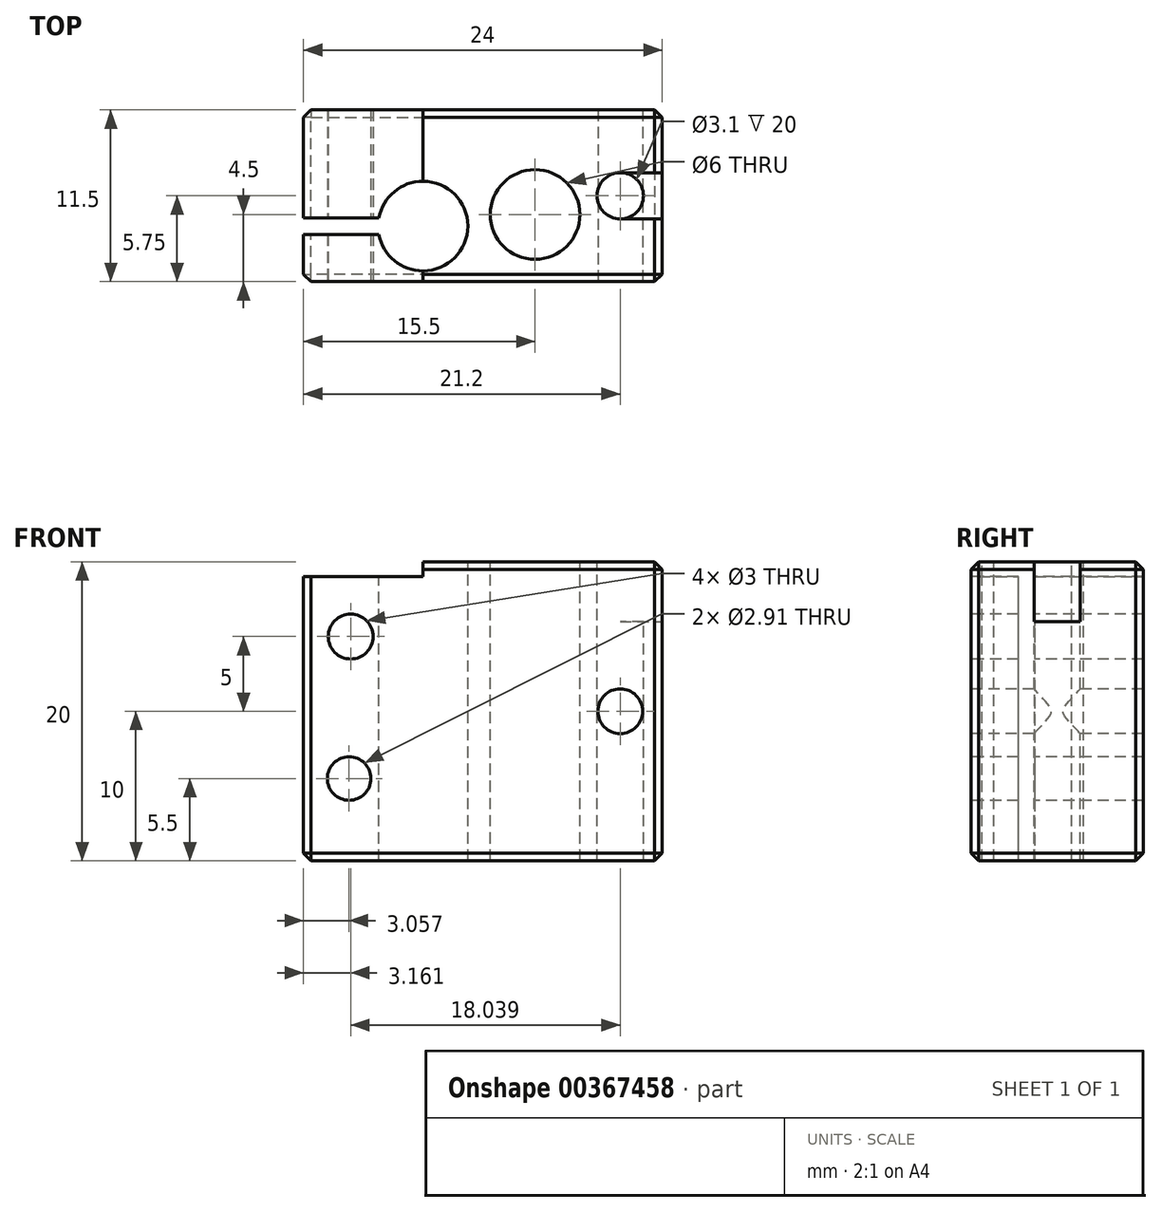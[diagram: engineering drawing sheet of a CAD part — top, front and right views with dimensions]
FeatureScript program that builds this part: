
annotation { "Feature Type Name" : "Feature", "Feature Type Description" : "" }
export const myFeature = defineFeature(function(context is Context, id is Id, definition is map)
    precondition{}
    {
        {
            var Q0;
            Q0=qCreatedBy(makeId("Top.planeOp"),FACE);
            var sketch = newSketch(context, id + "F0", { "sketchPlane" : qUnion([Q0])});
            skLineSegment(sketch, "E0.bottom", {"start": v(0, 0) * mm, "end": v(24, 0) * mm});
            skLineSegment(sketch, "E0.top", {"start": v(0, 11.5) * mm, "end": v(24, 11.5) * mm});
            skLineSegment(sketch, "E0.left", {"start": v(0, 0) * mm, "end": v(0, 11.5) * mm});
            skLineSegment(sketch, "E0.right", {"start": v(24, 0) * mm, "end": v(24, 11.5) * mm});
            skSolve(sketch);
        }
        {
            var Q0;
            Q0=qSketchRegion(id+"F0",true);
            extrude(context, id + "F1", {"entities" : qUnion([Q0]), "depth" : 20 * mm});
        }
        {
            var Q0;
            Q0=makeQuery(id+"F1.opExtrude","CAP_FACE",FACE,{"disambiguationData":[OSD([sQuery(id+"F0.wireOp",EDGE,"E0.bottom"),sQuery(id+"F0.wireOp",EDGE,"E0.top"),sQuery(id+"F0.wireOp",EDGE,"E0.left"),sQuery(id+"F0.wireOp",EDGE,"E0.right")])],"isStart":false});
            var sketch = newSketch(context, id + "F2", { "sketchPlane" : qUnion([Q0])});
            skCircle(sketch, "E1", {"center": v(21.2, 5.75) * mm, "radius": 1.55 * mm});
            skCircle(sketch, "E2", {"center": v(15.5, 4.5) * mm, "radius": 3 * mm});
            skCircle(sketch, "E3", {"center": v(8, 3.72) * mm, "radius": 3 * mm});
            skSolve(sketch);
        }
        {
            var Q0;
            Q0=makeQuery(id+"F2.imprint","IMPRINT",FACE,{"disambiguationData":[TD([[makeQuery(id+"F2.imprint","IMPRINT",EDGE,{"derivedFrom":sQuery(id+"F2.wireOp",EDGE,"E3")}),1.0]])]});
            var Q1;
            Q1=makeQuery(id+"F2.imprint","IMPRINT",FACE,{"disambiguationData":[TD([[makeQuery(id+"F2.imprint","IMPRINT",EDGE,{"derivedFrom":sQuery(id+"F2.wireOp",EDGE,"E2")}),1.0]])]});
            var Q2;
            Q2=makeQuery(id+"F2.imprint","IMPRINT",FACE,{"disambiguationData":[TD([[makeQuery(id+"F2.imprint","IMPRINT",EDGE,{"derivedFrom":sQuery(id+"F2.wireOp",EDGE,"E1")}),1.0]])]});
            var Q3;
            Q3=sQuery(id+"F2.wireOp",EDGE,"E2");
            var Q4;
            Q4=sQuery(id+"F2.wireOp",EDGE,"E1");
            var Q5;
            Q5=sQuery(id+"F2.wireOp",EDGE,"E3");
            extrude(context, id + "F3", {"entities" : qUnion([Q0, Q1, Q2]), "operationType" : NewBodyOperationType.REMOVE, "surfaceEntities" : qUnion([Q3, Q4, Q5]), "endBound" : BoundingType.THROUGH_ALL, "oppositeDirection" : true, "depth" : 25 * mm});
        }
        {
            var Q0;
            Q0=makeQuery(id+"F1.opExtrude","SWEPT_FACE",FACE,{"disambiguationData":[OSD([sQuery(id+"F0.wireOp",EDGE,"E0.bottom")])]});
            var sketch = newSketch(context, id + "F4", { "sketchPlane" : qUnion([Q0])});
            skCircle(sketch, "E4", {"center": v(21.2, 10) * mm, "radius": 1.5 * mm});
            skCircle(sketch, "E5", {"center": v(3.06, 5.5) * mm, "radius": 1.46 * mm});
            skCircle(sketch, "E6", {"center": v(3.16, 15) * mm, "radius": 1.5 * mm});
            skSolve(sketch);
        }
        {
            var Q0;
            Q0=qSketchRegion(id+"F4",true);
            extrude(context, id + "F5", {"entities" : qUnion([Q0]), "operationType" : NewBodyOperationType.REMOVE, "endBound" : BoundingType.THROUGH_ALL, "oppositeDirection" : true, "depth" : 25 * mm});
        }
        {
            var Q0;
            Q0=makeQuery(id+"F1.opExtrude","CAP_FACE",FACE,{"disambiguationData":[OSD([sQuery(id+"F0.wireOp",EDGE,"E0.bottom"),sQuery(id+"F0.wireOp",EDGE,"E0.top"),sQuery(id+"F0.wireOp",EDGE,"E0.left"),sQuery(id+"F0.wireOp",EDGE,"E0.right")])],"isStart":false});
            var sketch = newSketch(context, id + "F6", { "sketchPlane" : qUnion([Q0])});
            skLineSegment(sketch, "E7", {"start": v(21.2, 7.3) * mm, "end": v(24, 7.3) * mm});
            skLineSegment(sketch, "E8", {"start": v(21.2, 4.2) * mm, "end": v(24, 4.2) * mm});
            skSolve(sketch);
        }
        {
            var Q0;
            {var subQ0=sQuery(id+"F6.wireOp",EDGE,"E7");Q0=makeQuery(id+"F6.imprint","IMPRINT",FACE,{"disambiguationData":[TD([[makeQuery(id+"F6.imprint","IMPRINT",EDGE,{"derivedFrom":subQ0}),-1.0]])]});}
            extrude(context, id + "F7", {"entities" : qUnion([Q0]), "operationType" : NewBodyOperationType.REMOVE, "oppositeDirection" : true, "depth" : 4 * mm});
        }
        {
            var Q0;
            Q0=makeQuery(id+"F1.opExtrude","CAP_FACE",FACE,{"disambiguationData":[OSD([sQuery(id+"F0.wireOp",EDGE,"E0.bottom"),sQuery(id+"F0.wireOp",EDGE,"E0.top"),sQuery(id+"F0.wireOp",EDGE,"E0.left"),sQuery(id+"F0.wireOp",EDGE,"E0.right")])],"isStart":false});
            var sketch = newSketch(context, id + "F8", { "sketchPlane" : qUnion([Q0])});
            skLineSegment(sketch, "E9", {"start": v(8, 11.5) * mm, "end": v(8, 0) * mm});
            skSolve(sketch);
        }
        {
            var Q0;
            {var subQ0=makeQuery(id+"F1.opExtrude","CAP_EDGE",EDGE,{"disambiguationData":[OSD([sQuery(id+"F0.wireOp",EDGE,"E0.left")])],"isStart":false});Q0=makeQuery(id+"F8.imprint","IMPRINT",FACE,{"disambiguationData":[TD([[makeQuery(id+"F8.imprint","IMPRINT",EDGE,{"derivedFrom":subQ0}),-1.0]])]});}
            extrude(context, id + "F9", {"entities" : qUnion([Q0]), "operationType" : NewBodyOperationType.REMOVE, "oppositeDirection" : true, "depth" : 1 * mm});
        }
        {
            var Q0;
            Q0=makeQuery(id+"F9.boolean.opBoolean","COPY",EDGE,{"derivedFrom":makeQuery(id+"F9.opExtrude","CAP_EDGE",EDGE,{"disambiguationData":[OSD([sQuery(id+"F0.wireOp",EDGE,"E0.bottom")])],"isStart":false})});
            var Q1;
            Q1=makeQuery(id+"F9.boolean.opBoolean","COPY",EDGE,{"derivedFrom":makeQuery(id+"F9.opExtrude","CAP_EDGE",EDGE,{"disambiguationData":[OSD([sQuery(id+"F0.wireOp",EDGE,"E0.left")])],"isStart":false})});
            var Q2;
            Q2=makeQuery(id+"F1.opExtrude","SWEPT_EDGE",EDGE,{"disambiguationData":[OSD([sQuery(id+"F0.wireOp",EDGE,"E0.bottom"),sQuery(id+"F0.wireOp",EDGE,"E0.left")])]});
            var Q3;
            Q3=makeQuery(id+"F1.opExtrude","SWEPT_EDGE",EDGE,{"disambiguationData":[OSD([sQuery(id+"F0.wireOp",EDGE,"E0.top"),sQuery(id+"F0.wireOp",EDGE,"E0.left")])]});
            var Q4;
            {var subQ0=sQuery(id+"F8.wireOp",EDGE,"E9");Q4=makeQuery(id+"F9.boolean.opBoolean","COPY",EDGE,{"derivedFrom":makeQuery(id+"F9.opExtrude","CAP_EDGE",EDGE,{"disambiguationData":[OSD([subQ0]),TDD([makeQuery(id+"F8.imprint","IMPRINT",EDGE,{"disambiguationData":[TD([[makeQuery(id+"F8.imprint","INTERSECT",VERTEX,{"derivedFrom":[makeQuery(id+"F1.opExtrude","CAP_EDGE",EDGE,{"disambiguationData":[OSD([sQuery(id+"F0.wireOp",EDGE,"E0.top")])],"isStart":false}),subQ0]}),-1.0]])],"derivedFrom":subQ0})])],"isStart":true})});}
            var Q5;
            {var subQ0=sQuery(id+"F8.wireOp",EDGE,"E9");Q5=makeQuery(id+"F9.boolean.opBoolean","COPY",EDGE,{"derivedFrom":makeQuery(id+"F9.opExtrude","CAP_EDGE",EDGE,{"disambiguationData":[OSD([subQ0]),TDD([makeQuery(id+"F8.imprint","IMPRINT",EDGE,{"disambiguationData":[TD([[makeQuery(id+"F8.imprint","INTERSECT",VERTEX,{"derivedFrom":[makeQuery(id+"F1.opExtrude","CAP_EDGE",EDGE,{"disambiguationData":[OSD([sQuery(id+"F0.wireOp",EDGE,"E0.bottom")])],"isStart":false}),subQ0]}),1.0]])],"derivedFrom":subQ0})])],"isStart":true})});}
            var Q6;
            Q6=makeQuery(id+"F9.boolean.opBoolean","COPY",EDGE,{"derivedFrom":makeQuery(id+"F9.opExtrude","SWEPT_EDGE",EDGE,{"disambiguationData":[OSD([sQuery(id+"F0.wireOp",EDGE,"E0.bottom"),sQuery(id+"F8.wireOp",EDGE,"E9")])]})});
            var Q7;
            Q7=makeQuery(id+"F1.opExtrude","CAP_EDGE",EDGE,{"disambiguationData":[OSD([sQuery(id+"F0.wireOp",EDGE,"E0.bottom")])],"isStart":false});
            var Q8;
            {var subQ0=sQuery(id+"F0.wireOp",EDGE,"E0.bottom");var subQ1=sQuery(id+"F0.wireOp",EDGE,"E0.right");Q8=makeQuery(id+"F7.boolean.opBoolean","SPLIT",EDGE,{"disambiguationData":[TD([makeQuery(id+"F1.opExtrude","SWEPT_FACE",FACE,{"disambiguationData":[OSD([subQ0])]})])],"derivedFrom":makeQuery(id+"F1.opExtrude","CAP_EDGE",EDGE,{"disambiguationData":[OSD([subQ1])],"isStart":false})});}
            var Q9;
            Q9=makeQuery(id+"F7.boolean.opBoolean","COPY",EDGE,{"derivedFrom":makeQuery(id+"F7.opExtrude","CAP_EDGE",EDGE,{"disambiguationData":[OSD([sQuery(id+"F6.wireOp",EDGE,"E8")])],"isStart":true})});
            var Q10;
            {var subQ0=sQuery(id+"F0.wireOp",EDGE,"E0.right");var subQ1=sQuery(id+"F0.wireOp",EDGE,"E0.top");Q10=makeQuery(id+"F7.boolean.opBoolean","SPLIT",EDGE,{"disambiguationData":[TD([makeQuery(id+"F1.opExtrude","SWEPT_FACE",FACE,{"disambiguationData":[OSD([subQ1])]})])],"derivedFrom":makeQuery(id+"F1.opExtrude","CAP_EDGE",EDGE,{"disambiguationData":[OSD([subQ0])],"isStart":false})});}
            var Q11;
            Q11=makeQuery(id+"F1.opExtrude","CAP_EDGE",EDGE,{"disambiguationData":[OSD([sQuery(id+"F0.wireOp",EDGE,"E0.top")])],"isStart":false});
            var Q12;
            Q12=makeQuery(id+"F1.opExtrude","SWEPT_EDGE",EDGE,{"disambiguationData":[OSD([sQuery(id+"F0.wireOp",EDGE,"E0.bottom"),sQuery(id+"F0.wireOp",EDGE,"E0.right")])]});
            var Q13;
            Q13=makeQuery(id+"F1.opExtrude","CAP_EDGE",EDGE,{"disambiguationData":[OSD([sQuery(id+"F0.wireOp",EDGE,"E0.left")])],"isStart":true});
            var Q14;
            Q14=makeQuery(id+"F1.opExtrude","CAP_EDGE",EDGE,{"disambiguationData":[OSD([sQuery(id+"F0.wireOp",EDGE,"E0.bottom")])],"isStart":true});
            var Q15;
            Q15=makeQuery(id+"F1.opExtrude","CAP_EDGE",EDGE,{"disambiguationData":[OSD([sQuery(id+"F0.wireOp",EDGE,"E0.right")])],"isStart":true});
            var Q16;
            Q16=makeQuery(id+"F1.opExtrude","CAP_EDGE",EDGE,{"disambiguationData":[OSD([sQuery(id+"F0.wireOp",EDGE,"E0.top")])],"isStart":true});
            var Q17;
            Q17=makeQuery(id+"F1.opExtrude","SWEPT_EDGE",EDGE,{"disambiguationData":[OSD([sQuery(id+"F0.wireOp",EDGE,"E0.top"),sQuery(id+"F0.wireOp",EDGE,"E0.right")])]});
            var Q18;
            Q18=makeQuery(id+"F9.boolean.opBoolean","COPY",EDGE,{"derivedFrom":makeQuery(id+"F9.opExtrude","CAP_EDGE",EDGE,{"disambiguationData":[OSD([sQuery(id+"F0.wireOp",EDGE,"E0.top")])],"isStart":false})});
            var Q19;
            Q19=makeQuery(id+"F9.boolean.opBoolean","COPY",EDGE,{"derivedFrom":makeQuery(id+"F9.opExtrude","SWEPT_EDGE",EDGE,{"disambiguationData":[OSD([sQuery(id+"F0.wireOp",EDGE,"E0.top"),sQuery(id+"F8.wireOp",EDGE,"E9")])]})});
            var Q20;
            Q20=makeQuery(id+"F3.boolean.opBoolean","COPY",EDGE,{"derivedFrom":makeQuery(id+"F3.opExtrude","CAP_EDGE",EDGE,{"disambiguationData":[OSD([sQuery(id+"F2.wireOp",EDGE,"E2")])],"isStart":true})});
            chamfer(context, id + "F10", {"entities" : qUnion([Q0, Q1, Q2, Q3, Q4, Q5, Q6, Q7, Q8, Q9, Q10, Q11, Q12, Q13, Q14, Q15, Q16, Q17, Q18, Q19, Q20]), "width" : 0.5 * mm, "tangentPropagation" : true});
        }
        {
            var Q0;
            Q0=makeQuery(id+"F9.boolean.opBoolean","COPY",FACE,{"derivedFrom":makeQuery(id+"F9.opExtrude","CAP_FACE",FACE,{"disambiguationData":[OSD([sQuery(id+"F0.wireOp",EDGE,"E0.bottom"),sQuery(id+"F0.wireOp",EDGE,"E0.top"),sQuery(id+"F0.wireOp",EDGE,"E0.left"),sQuery(id+"F2.wireOp",EDGE,"E3"),sQuery(id+"F8.wireOp",EDGE,"E9")])],"isStart":false})});
            var sketch = newSketch(context, id + "F11", { "sketchPlane" : qUnion([Q0])});
            skLineSegment(sketch, "E10", {"start": v(10.63, 4.26) * mm, "end": v(-3.7, 4.26) * mm});
            skLineSegment(sketch, "E11", {"start": v(-3.7, 4.26) * mm, "end": v(-3.7, 3.16) * mm});
            skLineSegment(sketch, "E12", {"start": v(-3.7, 3.16) * mm, "end": v(10.63, 3.16) * mm});
            skLineSegment(sketch, "E13", {"start": v(10.63, 3.16) * mm, "end": v(10.63, 4.26) * mm});
            skSolve(sketch);
        }
        {
            var Q0;
            Q0=qSketchRegion(id+"F11",true);
            extrude(context, id + "F12", {"entities" : qUnion([Q0]), "operationType" : NewBodyOperationType.REMOVE, "endBound" : BoundingType.THROUGH_ALL, "oppositeDirection" : true, "depth" : 25 * mm});
        }
    });
